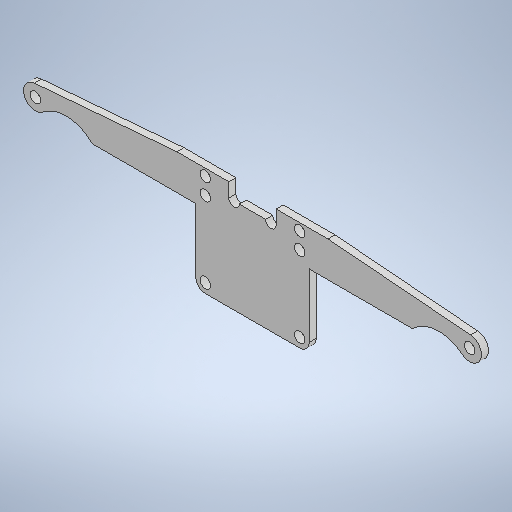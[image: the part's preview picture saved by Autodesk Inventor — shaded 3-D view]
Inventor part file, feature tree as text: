
AUTODESK INVENTOR PART (.ipt)
format: ipt  version: 2025.1 (Build 291241000, 241)  size: 302,080 bytes
history: native  units: mm
features: extrude x2, sketch x2, other x1
ambient origin geometry x8: Origin, YZ Plane, XZ Plane, XY Plane, X Axis, Y Axis, Z Axis, Center Point
bodies: Body1 (feature_tree)
feature tree (5):
  other  "ソリッド1"
  extrude  "押し出し1"  Depth=2.2mm
  extrude  "押し出し4"  Depth=5.0mm
  sketch  "スケッチ1"
  sketch  "スケッチ4"
